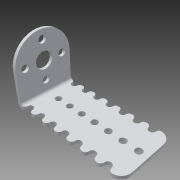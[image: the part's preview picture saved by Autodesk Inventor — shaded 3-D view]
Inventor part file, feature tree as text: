
AUTODESK INVENTOR PART (.ipt)
format: ipt  version: 2014 (Build 180170000, 170)  size: 283,136 bytes
history: native  units: mm
features: extrude x2, fillet x2, sketch x2
ambient origin geometry x8: Origin, YZ Plane, XZ Plane, XY Plane, X Axis, Y Axis, Z Axis, Center Point
bodies: Body1 (feature_tree)
feature tree (6):
  extrude  "Extrusión2"  Depth=25.0mm
  extrude  "Extrusión4"  Depth=14.0mm
  fillet  "Empalme1"  Radius=3.3mm
  fillet  "Empalme2"  Radius=40.0mm
  sketch  "Boceto2"  dims[d2=7.5mm d3=25.0mm]
  sketch  "Boceto4"  dims[d4=14.0mm d5=14.0mm d10=3.3mm d11=40.0mm d13=360.0deg d15=1.5mm d16=0.0mm d29=49.0mm d32=3.0mm d33=8.3mm d34=70.0mm d36=6.4mm d37=10.0mm d39=10.0mm d41=1.5mm d42=0.0mm d43=1.5mm d44=4.6mm d50=70.0mm d52=10.0mm d55=70.0mm d57=10.0mm d60=70.0mm d62=10.0mm d63=3.0mm d65=70.0mm d67=10.0mm d74=3.0mm d76=70.0mm d78=10.0mm d79=3.0mm d81=70.0mm d83=10.0mm d84=3.0mm d86=70.0mm d88=10.0mm d89=3.0mm d91=70.0mm d93=10.0mm d94=3.0mm d96=70.0mm d98=10.0mm d99=3.0mm d101=70.0mm d103=10.0mm d104=3.0mm d106=70.0mm d108=10.0mm d109=3.0mm d111=70.0mm d113=10.0mm d114=3.0mm d116=70.0mm d118=10.0mm d119=3.0mm d121=70.0mm d123=10.0mm d124=3.0mm d126=70.0mm d128=10.0mm d129=3.0mm d131=70.0mm d133=10.0mm d134=3.0mm d135=1.5mm d136=1.5mm d137=1.5mm d138=1.5mm d139=1.5mm d140=1.5mm d141=1.5mm d142=1.5mm d143=1.5mm d144=1.5mm d145=1.5mm d146=1.5mm d147=1.5mm d148=1.5mm d149=1.5mm d150=1.5mm d151=1.5mm]
